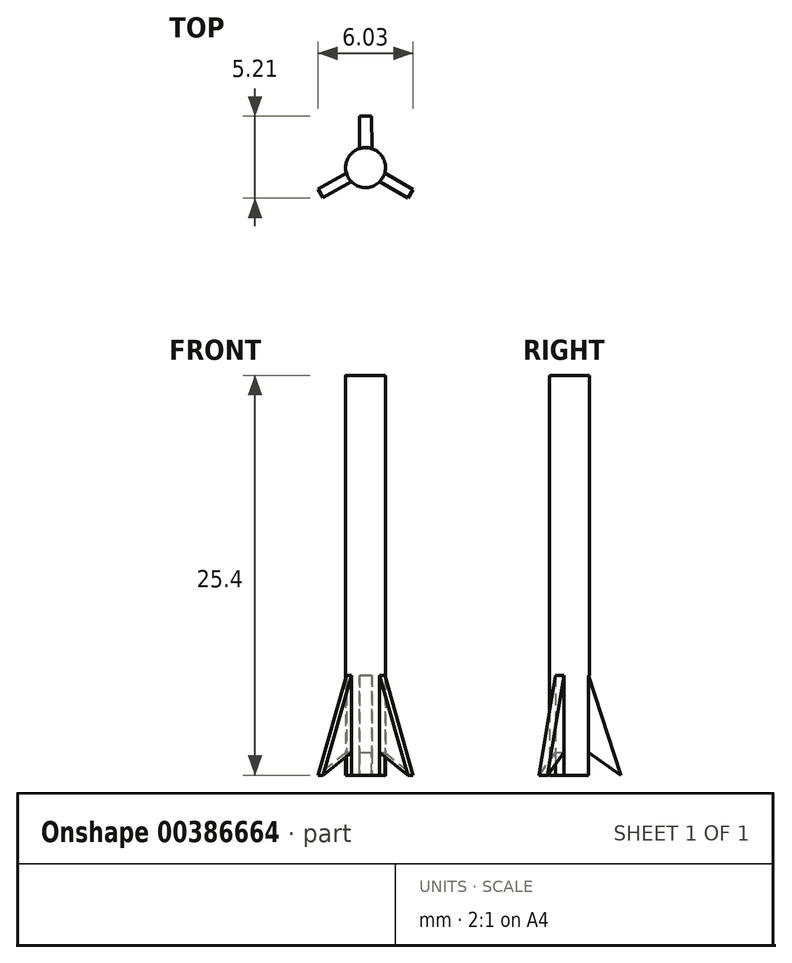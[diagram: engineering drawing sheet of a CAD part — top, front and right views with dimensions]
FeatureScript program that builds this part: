
annotation { "Feature Type Name" : "Feature", "Feature Type Description" : "" }
export const myFeature = defineFeature(function(context is Context, id is Id, definition is map)
    precondition{}
    {
        {
            var Q0;
            Q0=qCreatedBy(makeId("Top.planeOp"),FACE);
            var sketch = newSketch(context, id + "F0", { "sketchPlane" : qUnion([Q0])});
            skCircle(sketch, "E0", {"center": v(0, 0) * mm, "radius": 1.27 * mm});
            skLineSegment(sketch, "E1.top", {"start": v(9.66, -6.05) * mm, "end": v(9.98, -5.5) * mm});
            skLineSegment(sketch, "E1.left", {"start": v(0.9, -0.9) * mm, "end": v(9.66, -6.05) * mm});
            skLineSegment(sketch, "E1.right", {"start": v(1.22, -0.35) * mm, "end": v(9.98, -5.5) * mm});
            skLineSegment(sketch, "E2.top", {"start": v(-0.3, 11.37) * mm, "end": v(0.33, 11.36) * mm});
            skLineSegment(sketch, "E2.left", {"start": v(-0.4, 1.2) * mm, "end": v(-0.3, 11.37) * mm});
            skLineSegment(sketch, "E2.right", {"start": v(0.4, 1.2) * mm, "end": v(0.33, 11.36) * mm});
            skLineSegment(sketch, "E3.bottom", {"start": v(-1.22, -0.35) * mm, "end": v(-10.06, -5.35) * mm});
            skLineSegment(sketch, "E3.top", {"start": v(-0.9, -0.9) * mm, "end": v(-9.74, -5.9) * mm});
            skLineSegment(sketch, "E3.right", {"start": v(-10.06, -5.35) * mm, "end": v(-9.74, -5.9) * mm});
            skSolve(sketch);
        }
        {
            var Q0;
            {var subQ0=sQuery(id+"F0.wireOp",EDGE,"E0");var subQ4=makeQuery(id+"F0.imprint","INTERSECT",VERTEX,{"derivedFrom":[subQ0,sQuery(id+"F0.wireOp",EDGE,"E2.left")]});Q0=makeQuery(id+"F0.imprint","IMPRINT",FACE,{"disambiguationData":[TD([[makeQuery(id+"F0.imprint","IMPRINT",EDGE,{"disambiguationData":[TD([[subQ4,1.0]])],"derivedFrom":subQ0}),1.0]])]});}
            extrude(context, id + "F1", {"entities" : qUnion([Q0]), "depth" : 25.4 * mm});
        }
        {
            var Q0;
            {var subQ0=sQuery(id+"F0.wireOp",EDGE,"E3.bottom");Q0=makeQuery(id+"F0.imprint","IMPRINT",FACE,{"disambiguationData":[TD([[makeQuery(id+"F0.imprint","IMPRINT",EDGE,{"derivedFrom":subQ0}),1.0]])]});}
            var Q1;
            Q1=makeQuery(id+"F0.imprint","IMPRINT",FACE,{"disambiguationData":[TD([[makeQuery(id+"F0.imprint","IMPRINT",EDGE,{"derivedFrom":sQuery(id+"F0.wireOp",EDGE,"E2.top")}),-1.0]])]});
            var Q2;
            Q2=makeQuery(id+"F0.imprint","IMPRINT",FACE,{"disambiguationData":[TD([[makeQuery(id+"F0.imprint","IMPRINT",EDGE,{"derivedFrom":sQuery(id+"F0.wireOp",EDGE,"E1.top")}),1.0]])]});
            extrude(context, id + "F2", {"entities" : qUnion([Q0, Q1, Q2]), "operationType" : NewBodyOperationType.ADD, "depth" : 6.35 * mm});
        }
        {
            var Q0;
            Q0=makeQuery(id+"F2.opExtrude","SWEPT_FACE",FACE,{"disambiguationData":[OSD([sQuery(id+"F0.wireOp",EDGE,"E1.right")])]});
            var sketch = newSketch(context, id + "F3", { "sketchPlane" : qUnion([Q0])});
            skLineSegment(sketch, "E4", {"start": v(-1.23, 1.47) * mm, "end": v(-3.3, 0) * mm});
            skLineSegment(sketch, "E5", {"start": v(-3.3, 0) * mm, "end": v(-1.23, 6.35) * mm});
            skSolve(sketch);
        }
        {
            var Q0;
            {var subQ0=sQuery(id+"F3.wireOp",EDGE,"E5");Q0=makeQuery(id+"F3.imprint","IMPRINT",FACE,{"disambiguationData":[TD([[makeQuery(id+"F3.imprint","IMPRINT",EDGE,{"derivedFrom":subQ0}),1.0]])]});}
            extrude(context, id + "F4", {"entities" : qUnion([Q0]), "operationType" : NewBodyOperationType.REMOVE, "oppositeDirection" : true, "depth" : 25.4 * mm});
        }
        {
            var Q0;
            {var subQ0=sQuery(id+"F3.wireOp",EDGE,"E4");Q0=makeQuery(id+"F3.imprint","IMPRINT",FACE,{"disambiguationData":[TD([[makeQuery(id+"F3.imprint","IMPRINT",EDGE,{"derivedFrom":subQ0}),1.0]])]});}
            extrude(context, id + "F5", {"entities" : qUnion([Q0]), "operationType" : NewBodyOperationType.REMOVE, "oppositeDirection" : true, "depth" : 25.4 * mm});
        }
        {
            var Q0;
            Q0=makeQuery(id+"F2.opExtrude","SWEPT_FACE",FACE,{"disambiguationData":[OSD([sQuery(id+"F0.wireOp",EDGE,"E2.right")])]});
            var sketch = newSketch(context, id + "F6", { "sketchPlane" : qUnion([Q0])});
            skLineSegment(sketch, "E6", {"start": v(1.2, 1.46) * mm, "end": v(3.26, 0) * mm});
            skLineSegment(sketch, "E7", {"start": v(3.26, 0) * mm, "end": v(1.2, 6.35) * mm});
            skSolve(sketch);
        }
        {
            var Q0;
            {var subQ0=sQuery(id+"F6.wireOp",EDGE,"E7");Q0=makeQuery(id+"F6.imprint","IMPRINT",FACE,{"disambiguationData":[TD([[makeQuery(id+"F6.imprint","IMPRINT",EDGE,{"derivedFrom":subQ0}),-1.0]])]});}
            var Q1;
            {var subQ0=sQuery(id+"F6.wireOp",EDGE,"E6");Q1=makeQuery(id+"F6.imprint","IMPRINT",FACE,{"disambiguationData":[TD([[makeQuery(id+"F6.imprint","IMPRINT",EDGE,{"derivedFrom":subQ0}),-1.0]])]});}
            var Q2;
            Q2=makeQuery(id+"F2.opExtrude","SWEPT_FACE",FACE,{"disambiguationData":[OSD([sQuery(id+"F0.wireOp",EDGE,"E2.top")])]});
            var Q3;
            Q3=makeQuery(id+"F2.opExtrude","SWEPT_FACE",FACE,{"disambiguationData":[OSD([sQuery(id+"F0.wireOp",EDGE,"E2.left")])]});
            extrude(context, id + "F7", {"entities" : qUnion([Q0, Q1, Q2, Q3]), "operationType" : NewBodyOperationType.REMOVE, "oppositeDirection" : true, "depth" : 25.4 * mm});
        }
        {
            var Q0;
            Q0=makeQuery(id+"F2.opExtrude","SWEPT_FACE",FACE,{"disambiguationData":[OSD([sQuery(id+"F0.wireOp",EDGE,"E3.bottom")])]});
            var sketch = newSketch(context, id + "F8", { "sketchPlane" : qUnion([Q0])});
            skLineSegment(sketch, "E8", {"start": v(1.23, 1.46) * mm, "end": v(3.3, 0) * mm});
            skLineSegment(sketch, "E9", {"start": v(3.3, 0) * mm, "end": v(1.23, 6.35) * mm});
            skSolve(sketch);
        }
        {
            var Q0;
            {var subQ0=sQuery(id+"F8.wireOp",EDGE,"E9");Q0=makeQuery(id+"F8.imprint","IMPRINT",FACE,{"disambiguationData":[TD([[makeQuery(id+"F8.imprint","IMPRINT",EDGE,{"derivedFrom":subQ0}),-1.0]])]});}
            var Q1;
            {var subQ0=sQuery(id+"F8.wireOp",EDGE,"E8");Q1=makeQuery(id+"F8.imprint","IMPRINT",FACE,{"disambiguationData":[TD([[makeQuery(id+"F8.imprint","IMPRINT",EDGE,{"derivedFrom":subQ0}),-1.0]])]});}
            extrude(context, id + "F9", {"entities" : qUnion([Q0, Q1]), "operationType" : NewBodyOperationType.REMOVE, "oppositeDirection" : true, "depth" : 25.4 * mm});
        }
    });
